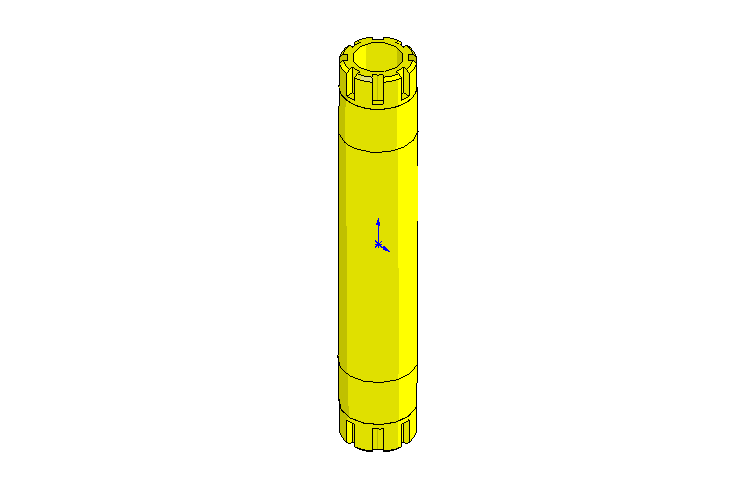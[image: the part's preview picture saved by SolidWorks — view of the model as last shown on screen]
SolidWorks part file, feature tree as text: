
SOLIDWORKS PART (.sldprt)
format: sldprt  version: not decoded by parser v0  size: 304,128 bytes
history: native  units: mm
features: plane x3, material x1, sketch x1, extrude x1, cut_revolve x1, chamfer x1, cut_extrude x1, pattern_circular x1, mirror x1 + 2 further entries (+10 scaffold rows collapsed)
feature tree (23):
  scaffold x10  (default folders/planes/origin — collapsed)
  material  "Matériau <non spécifié>"
  plane  "Plan de face"
  plane  "Plan de dessus"
  plane  "Plan de droite"
  sketch  "Esquisse1"  dims[D1=22.0mm D2=14.0mm]
  extrude  "Extrusion1"  Depth=126mm
  "Esquisse3"
  cut_revolve  "Enlèvement de matière-Révolution2"  Angle=360deg
  chamfer  "Chanfrein1"  Distance=1mm Angle=45deg
  "Esquisse4"
  cut_extrude  "Enlèv. mat.-Extru.1"  Depth=8.5mm
  pattern_circular  "Répétition circulaire1"  Count=8 Angle=45deg
  mirror  "Symétrie1"
decode coverage: 6 of 7 modeling features carry decoded parameters; 2 rows unclassified (native names shown)
note: suppression state not decoded; provenance and decode notes live in map.json
